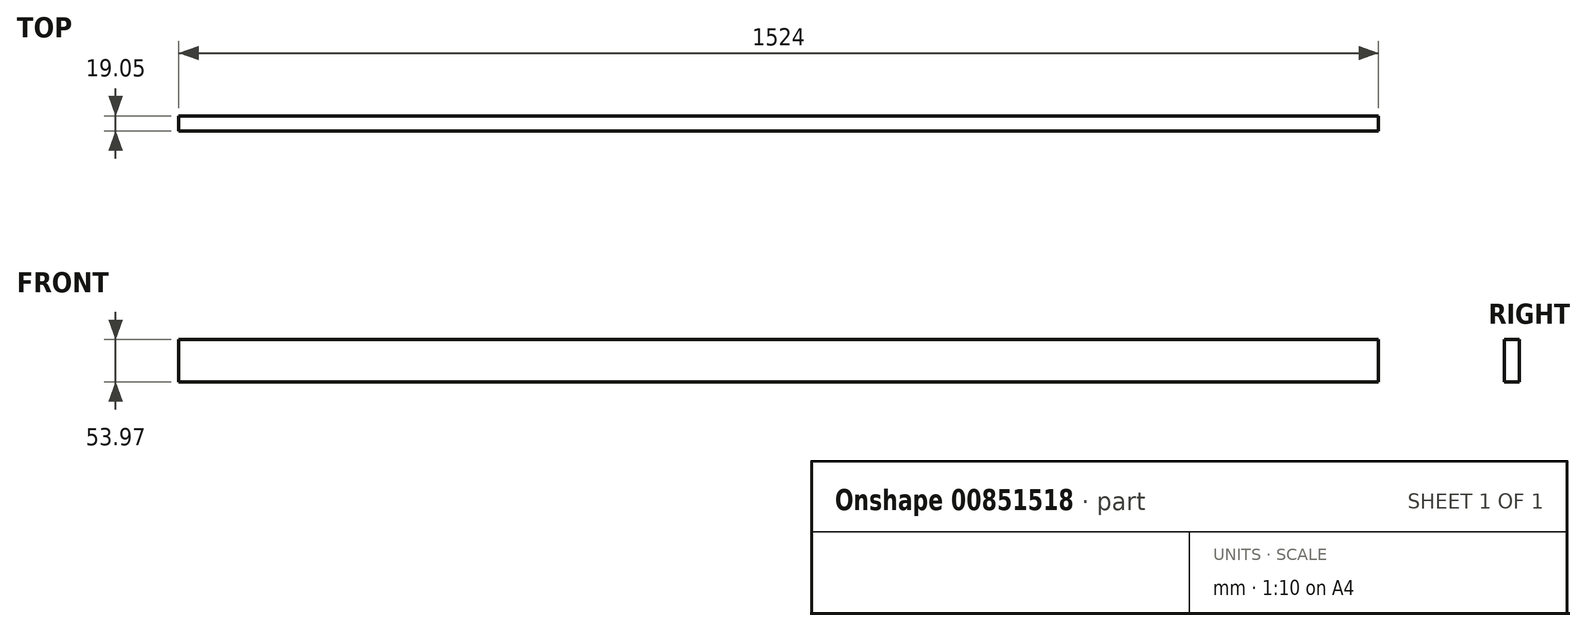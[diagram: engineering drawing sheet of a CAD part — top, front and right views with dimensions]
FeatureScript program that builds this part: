
annotation { "Feature Type Name" : "Feature", "Feature Type Description" : "" }
export const myFeature = defineFeature(function(context is Context, id is Id, definition is map)
    precondition{}
    {
        {
            var Q0;
            Q0=qCreatedBy(makeId("Front.planeOp"),FACE);
            var sketch = newSketch(context, id + "F0", { "sketchPlane" : qUnion([Q0])});
            skLineSegment(sketch, "E0.bottom", {"start": v(-301.75, 32.33) * mm, "end": v(1222.25, 32.33) * mm});
            skLineSegment(sketch, "E0.top", {"start": v(-301.75, -21.64) * mm, "end": v(1222.25, -21.64) * mm});
            skLineSegment(sketch, "E0.left", {"start": v(-301.75, 32.33) * mm, "end": v(-301.75, -21.64) * mm});
            skLineSegment(sketch, "E0.right", {"start": v(1222.25, 32.33) * mm, "end": v(1222.25, -21.64) * mm});
            skSolve(sketch);
        }
        {
            var Q0;
            Q0 = qSketchRegion(id + "F0", true);
            extrude(context, id + "F1", {"entities" : qUnion([Q0]), "depth" : 19.05 * mm, "offsetDistance" : 25.4 * mm});
        }
    });
